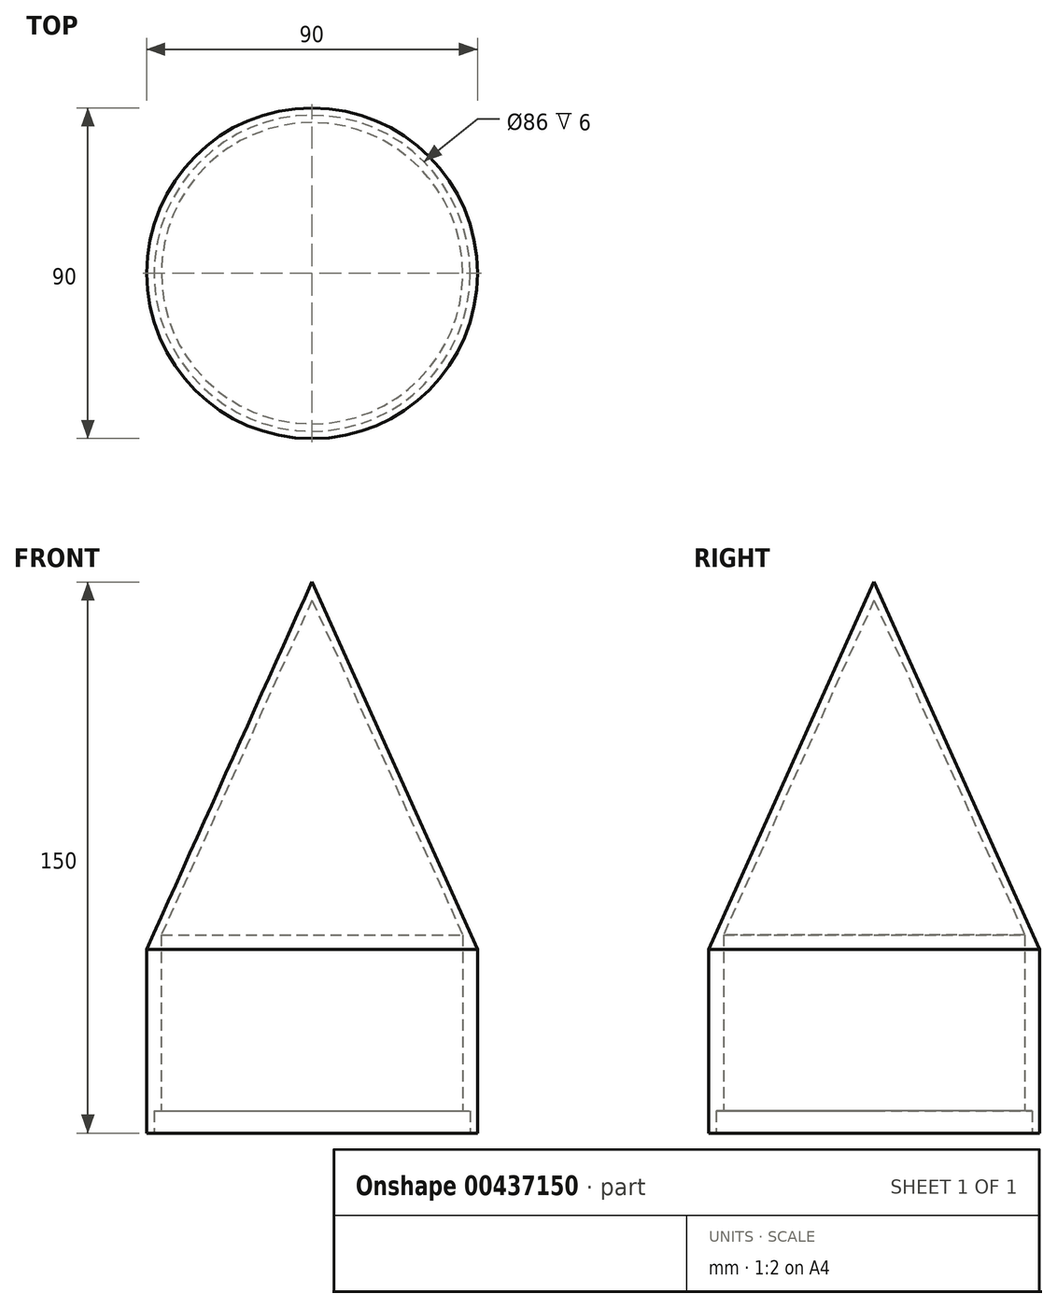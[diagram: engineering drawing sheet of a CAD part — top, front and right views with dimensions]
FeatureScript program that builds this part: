
annotation { "Feature Type Name" : "Feature", "Feature Type Description" : "" }
export const myFeature = defineFeature(function(context is Context, id is Id, definition is map)
    precondition{}
    {
        {
            var Q0;
            Q0=qCreatedBy(makeId("Front.planeOp"),FACE);
            var sketch = newSketch(context, id + "F0", { "sketchPlane" : qUnion([Q0])});
            skLineSegment(sketch, "E0", {"start": v(0, 0) * mm, "end": v(41, 0) * mm, "construction": true});
            skLineSegment(sketch, "E1", {"start": v(41, -26.48) * mm, "end": v(43, -26.48) * mm});
            skLineSegment(sketch, "E2", {"start": v(43, -26.48) * mm, "end": v(43, -32.48) * mm});
            skLineSegment(sketch, "E3", {"start": v(43, -32.48) * mm, "end": v(45, -32.48) * mm});
            skLineSegment(sketch, "E4", {"start": v(45, -32.48) * mm, "end": v(45, 17.52) * mm});
            skLineSegment(sketch, "E5", {"start": v(45, 17.52) * mm, "end": v(0, 117.52) * mm});
            skLineSegment(sketch, "E6", {"start": v(41, 17.52) * mm, "end": v(0, 17.52) * mm, "construction": true});
            skLineSegment(sketch, "E7", {"start": v(0, 17.52) * mm, "end": v(0, 117.52) * mm, "construction": true});
            skLineSegment(sketch, "E8", {"start": v(0, 117.52) * mm, "end": v(0, 112.52) * mm});
            skLineSegment(sketch, "E9", {"start": v(0, 112.52) * mm, "end": v(41, 21.41) * mm});
            skLineSegment(sketch, "E10", {"start": v(41, -26.48) * mm, "end": v(41, 21.41) * mm});
            skSolve(sketch);
        }
        {
            var Q0;
            Q0=makeQuery(id+"F0.imprint","IMPRINT",FACE,{"disambiguationData":[TD([[makeQuery(id+"F0.imprint","IMPRINT",EDGE,{"derivedFrom":sQuery(id+"F0.wireOp",EDGE,"E1")}),1.0]])]});
            var Q1;
            Q1=sQuery(id+"F0.wireOp",EDGE,"E7");
            revolve(context, id + "F1", {"entities" : qUnion([Q0]), "axis" : qUnion([Q1]), "revolveType" : RevolveType.FULL});
        }
    });
